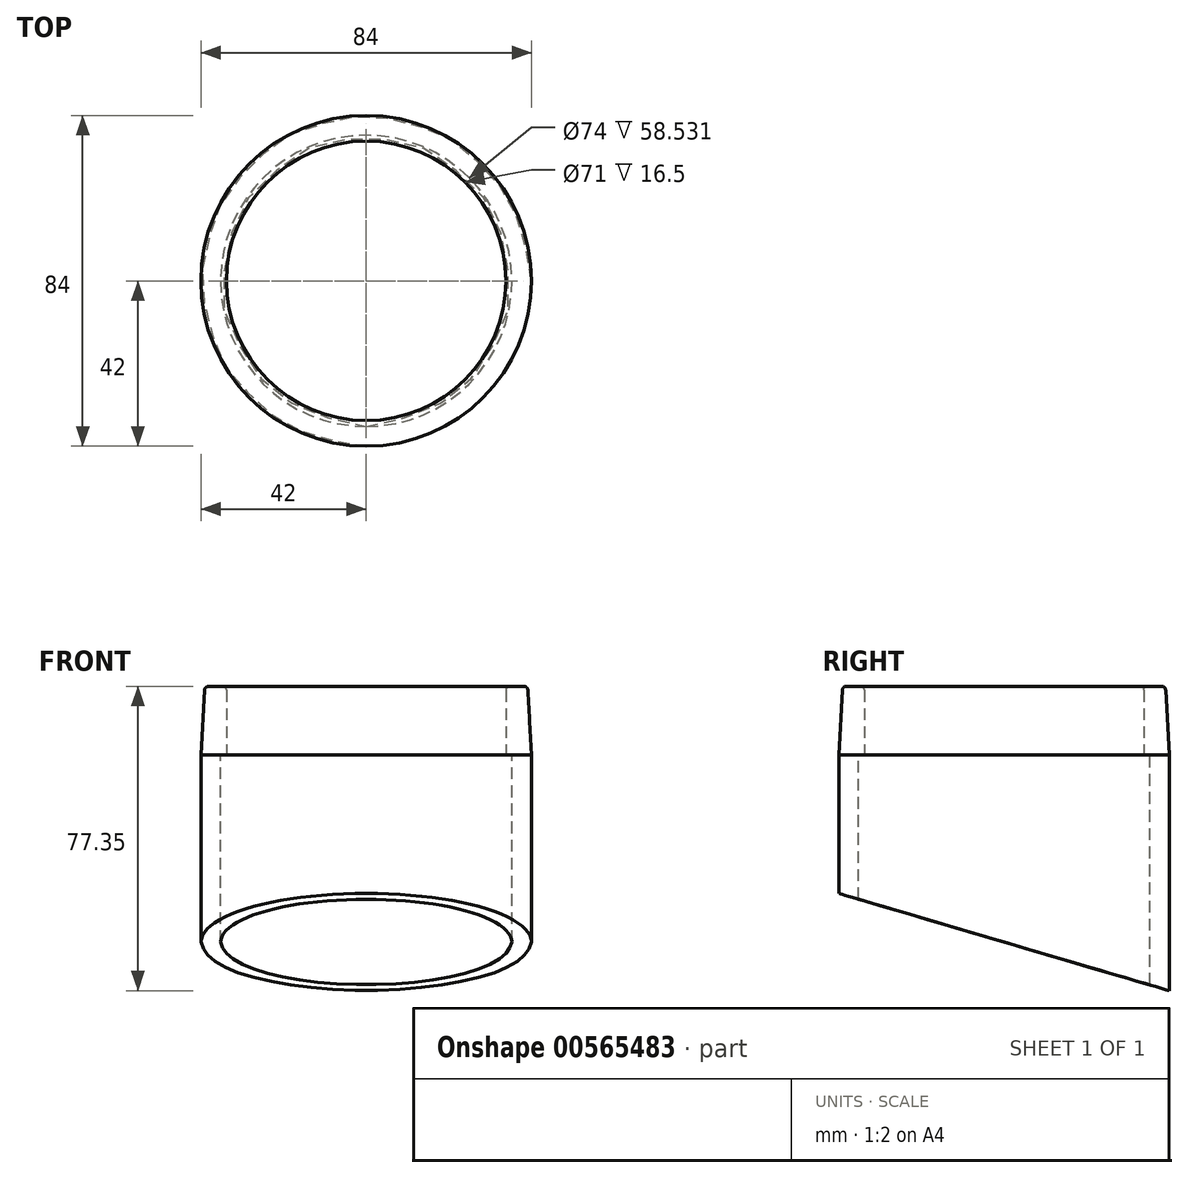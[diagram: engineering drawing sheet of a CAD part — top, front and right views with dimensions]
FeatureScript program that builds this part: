
annotation { "Feature Type Name" : "Feature", "Feature Type Description" : "" }
export const myFeature = defineFeature(function(context is Context, id is Id, definition is map)
    precondition{}
    {
        {
            var Q0;
            Q0=qCreatedBy(makeId("Top.planeOp"),FACE);
            var sketch = newSketch(context, id + "F0", { "sketchPlane" : qUnion([Q0])});
            skCircle(sketch, "E0", {"center": v(0, 0) * mm, "radius": 42 * mm});
            skCircle(sketch, "E1", {"center": v(0, 0) * mm, "radius": 35.5 * mm});
            skSolve(sketch);
        }
        {
            var Q0;
            Q0=makeQuery(id+"F0.imprint","IMPRINT",FACE,{"disambiguationData":[TD([[makeQuery(id+"F0.imprint","IMPRINT",EDGE,{"derivedFrom":sQuery(id+"F0.wireOp",EDGE,"E0")}),1.0]])]});
            extrude(context, id + "F1", {"entities" : qUnion([Q0]), "depth" : 17.5 * mm, "offsetDistance" : 25 * mm});
        }
        {
            var Q0;
            Q0=makeQuery(id+"F1.opExtrude","CAP_EDGE",EDGE,{"disambiguationData":[OSD([sQuery(id+"F0.wireOp",EDGE,"E0")])],"isStart":false});
            chamfer(context, id + "F2", {"entities" : qUnion([Q0]), "chamferType" : ChamferType.TWO_OFFSETS, "width1" : 1 * mm, "oppositeDirection" : false, "width2" : 17.5 * mm, "tangentPropagation" : true});
        }
        {
            var Q0;
            {var subQ0=sQuery(id+"F0.wireOp",EDGE,"E0");Q0=makeQuery(id+"F2.opChamfer","BLEND_EDGE",EDGE,{"blendedFrom":[makeQuery(id+"F1.opExtrude","CAP_EDGE",EDGE,{"disambiguationData":[OSD([subQ0])],"isStart":false}),makeQuery(id+"F1.opExtrude","CAP_FACE",FACE,{"disambiguationData":[OSD([subQ0,sQuery(id+"F0.wireOp",EDGE,"E1")])],"isStart":false})],"blendedInto":[makeQuery(id+"F1.opExtrude","CAP_FACE",FACE,{"disambiguationData":[OSD([subQ0,sQuery(id+"F0.wireOp",EDGE,"E1")])],"isStart":false})]});}
            var Q1;
            Q1=makeQuery(id+"F1.opExtrude","CAP_EDGE",EDGE,{"disambiguationData":[OSD([sQuery(id+"F0.wireOp",EDGE,"E1")])],"isStart":false});
            fillet(context, id + "F3", {"entities" : qUnion([Q0, Q1]), "radius" : 1 * mm, "tangentPropagation" : true, "allowEdgeOverflow" : false});
        }
        {
            var Q0;
            Q0=makeQuery(id+"F1.opExtrude","CAP_FACE",FACE,{"disambiguationData":[OSD([sQuery(id+"F0.wireOp",EDGE,"E0"),sQuery(id+"F0.wireOp",EDGE,"E1")])],"isStart":true});
            var sketch = newSketch(context, id + "F4", { "sketchPlane" : qUnion([Q0])});
            skCircle(sketch, "E2", {"center": v(0, 0) * mm, "radius": 42 * mm});
            skCircle(sketch, "E3", {"center": v(0, 0) * mm, "radius": 37 * mm});
            skSolve(sketch);
        }
        {
            var Q0;
            Q0=makeQuery(id+"F4.imprint","IMPRINT",FACE,{"disambiguationData":[TD([[makeQuery(id+"F4.imprint","IMPRINT",EDGE,{"derivedFrom":sQuery(id+"F4.wireOp",EDGE,"E3")}),-1.0]])]});
            extrude(context, id + "F5", {"entities" : qUnion([Q0]), "depth" : 60 * mm, "offsetDistance" : 25 * mm});
        }
        {
            var Q0;
            Q0=qCreatedBy(makeId("Right.planeOp"),FACE);
            var sketch = newSketch(context, id + "F6", { "sketchPlane" : qUnion([Q0])});
            skLineSegment(sketch, "E4", {"start": v(42.5, -60) * mm, "end": v(-42.5, -35) * mm});
            skLineSegment(sketch, "E5.bottom", {"start": v(42.5, 0) * mm, "end": v(-42.5, 0) * mm});
            skLineSegment(sketch, "E6", {"start": v(-42.5, -35) * mm, "end": v(-42.5, 0) * mm});
            skLineSegment(sketch, "E7", {"start": v(42.5, -60) * mm, "end": v(42.5, 0) * mm});
            skLineSegment(sketch, "E8", {"start": v(42.5, -60) * mm, "end": v(42.5, -69.37) * mm});
            skLineSegment(sketch, "E9", {"start": v(42.5, -69.37) * mm, "end": v(-49.79, -69.37) * mm});
            skLineSegment(sketch, "E10", {"start": v(-49.79, -69.37) * mm, "end": v(-42.5, -35) * mm});
            skSolve(sketch);
        }
        {
            var Q0;
            Q0=makeQuery(id+"F6.imprint","IMPRINT",FACE,{"disambiguationData":[TD([[makeQuery(id+"F6.imprint","IMPRINT",EDGE,{"derivedFrom":sQuery(id+"F6.wireOp",EDGE,"E4")}),1.0]])]});
            extrude(context, id + "F7", {"entities" : qUnion([Q0]), "operationType" : NewBodyOperationType.REMOVE, "endBound" : BoundingType.SYMMETRIC, "oppositeDirection" : true, "depth" : 90 * mm, "offsetDistance" : 25 * mm});
        }
    });
